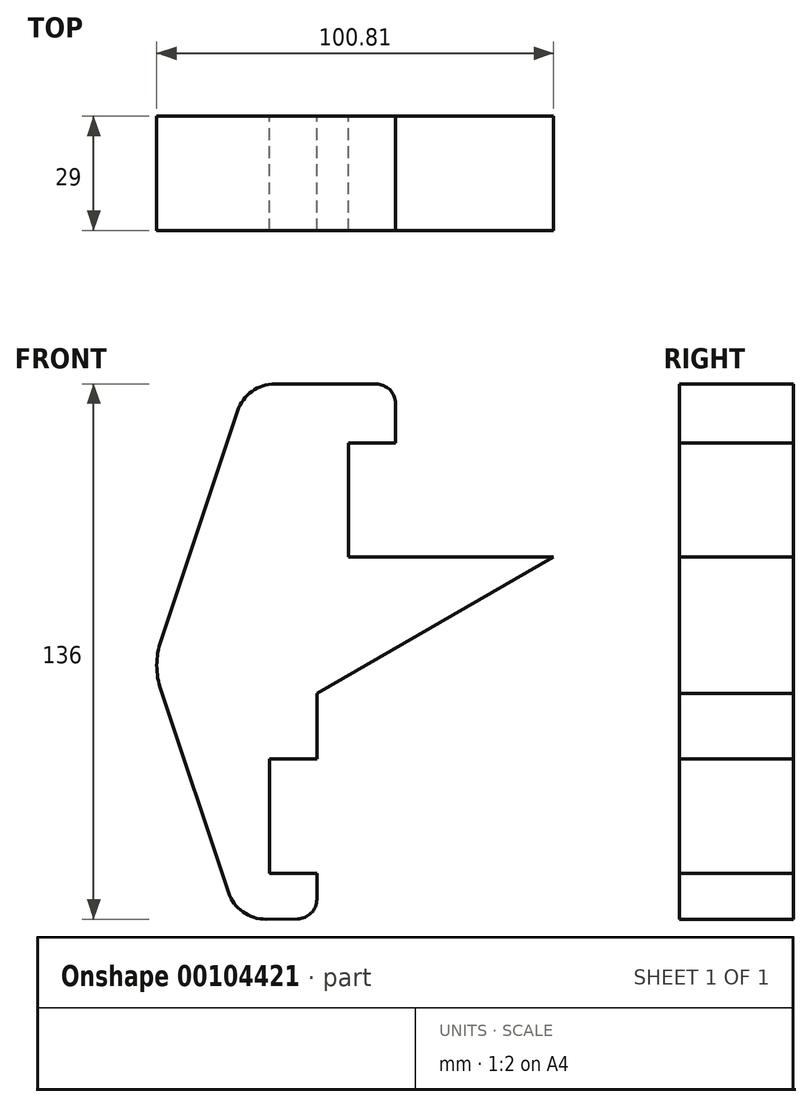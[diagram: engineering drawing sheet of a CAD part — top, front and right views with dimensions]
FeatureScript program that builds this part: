
annotation { "Feature Type Name" : "Feature", "Feature Type Description" : "" }
export const myFeature = defineFeature(function(context is Context, id is Id, definition is map)
    precondition{}
    {
        {
            var Q0;
            Q0=qCreatedBy(makeId("Front.planeOp"),FACE);
            var sketch = newSketch(context, id + "F0", { "sketchPlane" : qUnion([Q0])});
            skLineSegment(sketch, "E0", {"start": v(15, 71.5) * mm, "end": v(-10.63, 71.5) * mm});
            skLineSegment(sketch, "E1", {"start": v(-20.12, 64.67) * mm, "end": v(-39.63, 6.35) * mm});
            skLineSegment(sketch, "E2", {"start": v(36.06, 0) * mm, "end": v(-77.4, 0) * mm, "construction": true});
            skLineSegment(sketch, "E3.MirrorCS", {"start": v(-22.46, -57.67) * mm, "end": v(-39.63, -6.35) * mm});
            skLineSegment(sketch, "E4.MirrorCS", {"start": v(-4.95, -64.42) * mm, "end": v(-12.87, -64.5) * mm});
            skLineSegment(sketch, "E5.MirrorCS", {"start": v(0, -52.83) * mm, "end": v(0, -59.42) * mm});
            skLineSegment(sketch, "E6.MirrorCS", {"start": v(-12, -52.83) * mm, "end": v(0, -52.83) * mm});
            skLineSegment(sketch, "E7.MirrorCS", {"start": v(-12, -23.83) * mm, "end": v(-12, -52.83) * mm});
            skLineSegment(sketch, "E8.MirrorCS", {"start": v(0, -23.83) * mm, "end": v(-12, -23.83) * mm});
            skPoint(sketch, "E9.visualSharp", {"position": v(-17.83, 71.5) * mm});
            skArc(sketch, "E9.filletArc", {"start": v(-10.63, 71.5) * mm, "mid": v(-16.48, 69.62) * mm, "end": v(-20.12, 64.67) * mm});
            skPoint(sketch, "E10.visualSharp", {"position": v(-41.76, 0) * mm});
            skArc(sketch, "E10.filletArc", {"start": v(-39.63, 6.35) * mm, "mid": v(-40.67, 0) * mm, "end": v(-39.63, -6.35) * mm});
            skPoint(sketch, "E11.visualSharp", {"position": v(-20.15, -64.57) * mm});
            skArc(sketch, "E11.filletArc", {"start": v(-22.46, -57.67) * mm, "mid": v(-18.78, -62.65) * mm, "end": v(-12.87, -64.5) * mm});
            skPoint(sketch, "E12.visualSharp", {"position": v(0, -64.36) * mm});
            skArc(sketch, "E12.filletArc", {"start": v(-4.95, -64.42) * mm, "mid": v(-1.45, -62.93) * mm, "end": v(0, -59.42) * mm});
            skLineSegment(sketch, "E13", {"start": v(60.14, 27.5) * mm, "end": v(0, -7.18) * mm});
            skLineSegment(sketch, "E14", {"start": v(0, -7.18) * mm, "end": v(0, -23.83) * mm});
            skLineSegment(sketch, "E15", {"start": v(60.14, 27.5) * mm, "end": v(8, 27.5) * mm});
            skLineSegment(sketch, "E16", {"start": v(8, 27.5) * mm, "end": v(8, 56.5) * mm});
            skLineSegment(sketch, "E17", {"start": v(8, 56.5) * mm, "end": v(20, 56.5) * mm});
            skLineSegment(sketch, "E18", {"start": v(20, 56.5) * mm, "end": v(20, 66.5) * mm});
            skPoint(sketch, "E19.visualSharp", {"position": v(20, 71.5) * mm});
            skArc(sketch, "E19.filletArc", {"start": v(20, 66.5) * mm, "mid": v(18.54, 70.04) * mm, "end": v(15, 71.5) * mm});
            skSolve(sketch);
        }
        {
            var Q0;
            Q0 = qSketchRegion(id + "F0", true);
            extrude(context, id + "F1", {"entities" : qUnion([Q0]), "depth" : 29 * mm, "offsetDistance" : 25 * mm});
        }
    });
